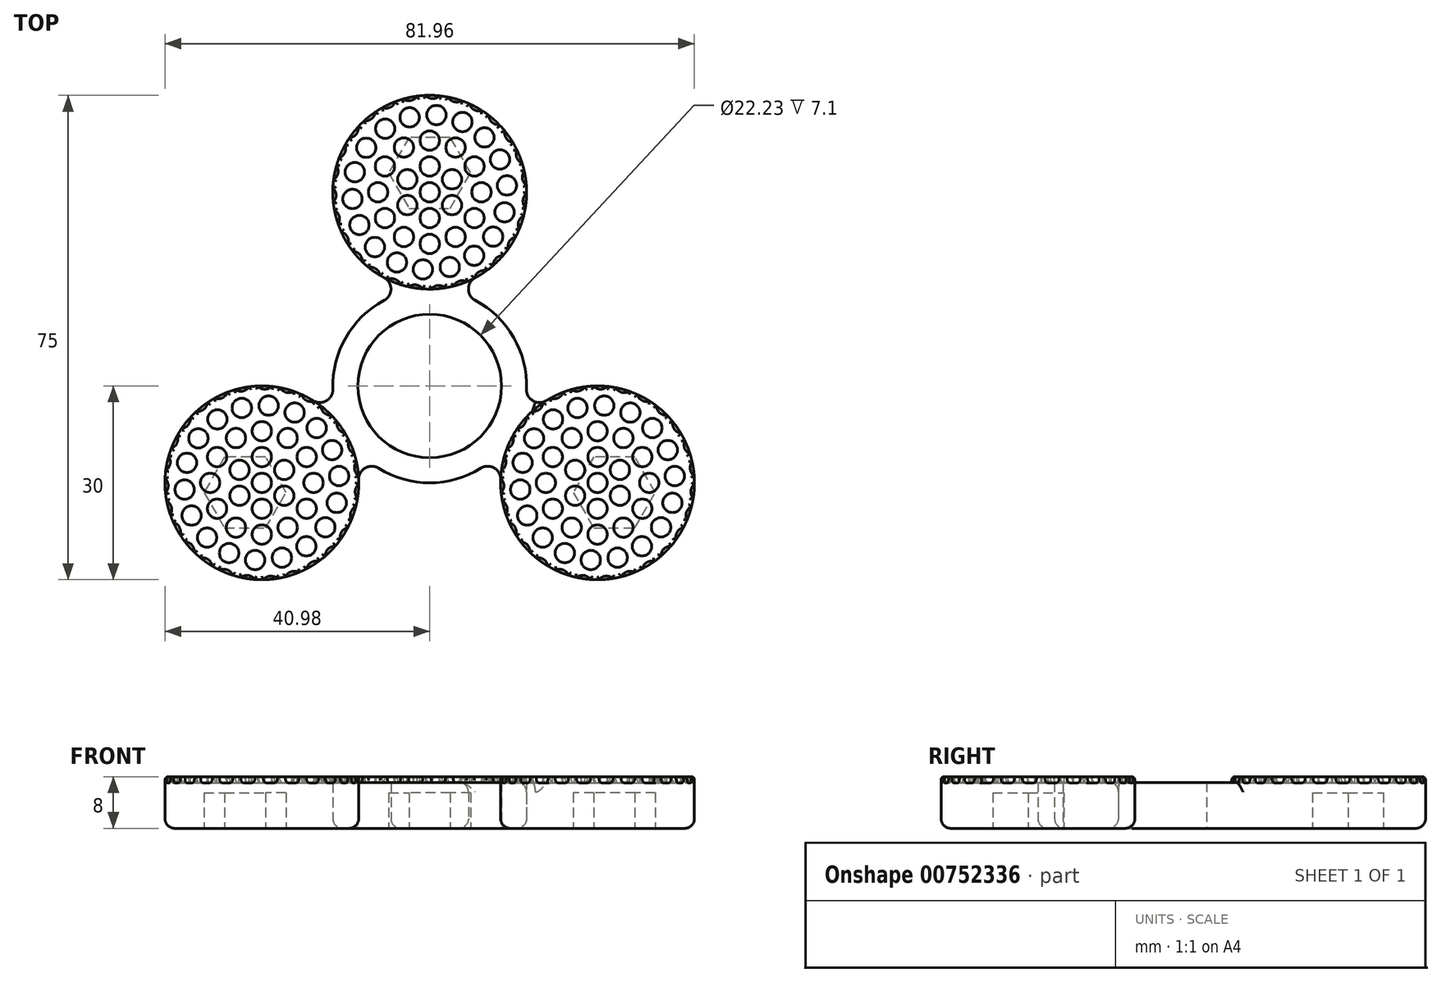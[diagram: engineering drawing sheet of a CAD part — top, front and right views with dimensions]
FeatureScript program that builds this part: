
annotation { "Feature Type Name" : "Feature", "Feature Type Description" : "" }
export const myFeature = defineFeature(function(context is Context, id is Id, definition is map)
    precondition{}
    {
        {
            var Q0;
            Q0=qCreatedBy(makeId("Top.planeOp"),FACE);
            var sketch = newSketch(context, id + "F0", { "sketchPlane" : qUnion([Q0])});
            skCircle(sketch, "E0", {"center": v(0, 0) * mm, "radius": 15 * mm});
            skSolve(sketch);
        }
        {
            var Q0;
            Q0 = qSketchRegion(id + "F0", true);
            extrude(context, id + "F1", {"entities" : qUnion([Q0]), "depth" : 8 * mm, "offsetDistance" : 25 * mm});
        }
        {
            var Q0;
            Q0=makeQuery(id+"F1.opExtrude","CAP_FACE",FACE,{"disambiguationData":[OSD([sQuery(id+"F0.wireOp",EDGE,"E0")])],"isStart":false});
            var sketch = newSketch(context, id + "F2", { "sketchPlane" : qUnion([Q0])});
            skCircle(sketch, "E1", {"center": v(0, 0) * mm, "radius": 1.5 * mm});
            skCircle(sketch, "E2", {"center": v(0, 4) * mm, "radius": 1.5 * mm});
            skCircle(sketch, "E3.1.0", {"center": v(-3.46, 2) * mm, "radius": 1.5 * mm});
            skCircle(sketch, "E3.2.0", {"center": v(-3.46, -2) * mm, "radius": 1.5 * mm});
            skCircle(sketch, "E3.3.0", {"center": v(0, -4) * mm, "radius": 1.5 * mm});
            skCircle(sketch, "E3.4.0", {"center": v(3.46, -2) * mm, "radius": 1.5 * mm});
            skCircle(sketch, "E3.5.0", {"center": v(3.46, 2) * mm, "radius": 1.5 * mm});
            skCircle(sketch, "E4", {"center": v(4, 6.93) * mm, "radius": 1.5 * mm});
            skCircle(sketch, "E5.1.0", {"center": v(0, 8) * mm, "radius": 1.5 * mm});
            skCircle(sketch, "E5.2.0", {"center": v(-4, 6.93) * mm, "radius": 1.5 * mm});
            skCircle(sketch, "E5.3.0", {"center": v(-6.93, 4) * mm, "radius": 1.5 * mm});
            skCircle(sketch, "E5.4.0", {"center": v(-8, 0) * mm, "radius": 1.5 * mm});
            skCircle(sketch, "E5.5.0", {"center": v(-6.93, -4) * mm, "radius": 1.5 * mm});
            skCircle(sketch, "E5.6.0", {"center": v(-4, -6.93) * mm, "radius": 1.5 * mm});
            skCircle(sketch, "E5.7.0", {"center": v(0, -8) * mm, "radius": 1.5 * mm});
            skCircle(sketch, "E5.8.0", {"center": v(4, -6.93) * mm, "radius": 1.5 * mm});
            skCircle(sketch, "E5.9.0", {"center": v(6.93, -4) * mm, "radius": 1.5 * mm});
            skCircle(sketch, "E5.10.0", {"center": v(8, 0) * mm, "radius": 1.5 * mm});
            skCircle(sketch, "E5.11.0", {"center": v(6.93, 4) * mm, "radius": 1.5 * mm});
            skCircle(sketch, "E6", {"center": v(8.49, 8.49) * mm, "radius": 1.5 * mm});
            skCircle(sketch, "E7.1.0", {"center": v(5.07, 10.88) * mm, "radius": 1.5 * mm});
            skCircle(sketch, "E7.2.0", {"center": v(1.05, 11.95) * mm, "radius": 1.5 * mm});
            skCircle(sketch, "E7.3.0", {"center": v(-3.1, 11.6) * mm, "radius": 1.5 * mm});
            skCircle(sketch, "E7.4.0", {"center": v(-6.88, 9.83) * mm, "radius": 1.5 * mm});
            skCircle(sketch, "E7.5.0", {"center": v(-9.83, 6.88) * mm, "radius": 1.5 * mm});
            skCircle(sketch, "E7.6.0", {"center": v(-11.6, 3.1) * mm, "radius": 1.5 * mm});
            skCircle(sketch, "E7.7.0", {"center": v(-11.95, -1.05) * mm, "radius": 1.5 * mm});
            skCircle(sketch, "E7.8.0", {"center": v(-10.88, -5.07) * mm, "radius": 1.5 * mm});
            skCircle(sketch, "E7.9.0", {"center": v(-8.49, -8.49) * mm, "radius": 1.5 * mm});
            skCircle(sketch, "E7.10.0", {"center": v(-5.07, -10.88) * mm, "radius": 1.5 * mm});
            skCircle(sketch, "E7.11.0", {"center": v(-1.05, -11.95) * mm, "radius": 1.5 * mm});
            skCircle(sketch, "E7.12.0", {"center": v(3.1, -11.6) * mm, "radius": 1.5 * mm});
            skCircle(sketch, "E7.13.0", {"center": v(6.88, -9.83) * mm, "radius": 1.5 * mm});
            skCircle(sketch, "E7.14.0", {"center": v(9.83, -6.88) * mm, "radius": 1.5 * mm});
            skCircle(sketch, "E7.15.0", {"center": v(11.6, -3.1) * mm, "radius": 1.5 * mm});
            skCircle(sketch, "E7.16.0", {"center": v(11.95, 1.05) * mm, "radius": 1.5 * mm});
            skCircle(sketch, "E7.17.0", {"center": v(10.88, 5.07) * mm, "radius": 1.5 * mm});
            skArc(sketch, "E8", {"start": v(12.88, 7.7) * mm, "mid": v(12.29, 8.6) * mm, "end": v(11.63, 9.47) * mm});
            skArc(sketch, "E9", {"start": v(11.63, 9.47) * mm, "mid": v(11.88, 8.32) * mm, "end": v(12.88, 7.7) * mm});
            skArc(sketch, "E10.1.0", {"start": v(9.14, 11.9) * mm, "mid": v(9.64, 10.83) * mm, "end": v(10.75, 10.46) * mm});
            skArc(sketch, "E10.1.1", {"start": v(10.75, 10.46) * mm, "mid": v(9.97, 11.2) * mm, "end": v(9.14, 11.9) * mm});
            skArc(sketch, "E10.2.0", {"start": v(6.15, 13.68) * mm, "mid": v(6.88, 12.76) * mm, "end": v(8.05, 12.66) * mm});
            skArc(sketch, "E10.2.1", {"start": v(8.05, 12.66) * mm, "mid": v(7.12, 13.2) * mm, "end": v(6.15, 13.68) * mm});
            skArc(sketch, "E10.3.0", {"start": v(2.83, 14.73) * mm, "mid": v(3.75, 14) * mm, "end": v(4.92, 14.17) * mm});
            skArc(sketch, "E10.3.1", {"start": v(4.92, 14.17) * mm, "mid": v(3.88, 14.49) * mm, "end": v(2.83, 14.73) * mm});
            skArc(sketch, "E10.4.0", {"start": v(-0.65, 14.99) * mm, "mid": v(0.42, 14.5) * mm, "end": v(1.52, 14.92) * mm});
            skArc(sketch, "E10.4.1", {"start": v(1.52, 14.92) * mm, "mid": v(0.44, 15) * mm, "end": v(-0.65, 14.99) * mm});
            skArc(sketch, "E10.5.0", {"start": v(-4.08, 14.43) * mm, "mid": v(-2.93, 14.2) * mm, "end": v(-1.97, 14.87) * mm});
            skArc(sketch, "E10.5.1", {"start": v(-1.97, 14.87) * mm, "mid": v(-3.03, 14.7) * mm, "end": v(-4.08, 14.43) * mm});
            skArc(sketch, "E10.6.0", {"start": v(-7.3, 13.1) * mm, "mid": v(-6.13, 13.14) * mm, "end": v(-5.34, 14.02) * mm});
            skArc(sketch, "E10.6.1", {"start": v(-5.34, 14.02) * mm, "mid": v(-6.34, 13.6) * mm, "end": v(-7.3, 13.1) * mm});
            skArc(sketch, "E10.7.0", {"start": v(-10.13, 11.06) * mm, "mid": v(-9, 11.37) * mm, "end": v(-8.43, 12.4) * mm});
            skArc(sketch, "E10.7.1", {"start": v(-8.43, 12.4) * mm, "mid": v(-9.3, 11.77) * mm, "end": v(-10.13, 11.06) * mm});
            skArc(sketch, "E10.8.0", {"start": v(-12.4, 8.43) * mm, "mid": v(-11.37, 9) * mm, "end": v(-11.06, 10.13) * mm});
            skArc(sketch, "E10.8.1", {"start": v(-11.06, 10.13) * mm, "mid": v(-11.77, 9.3) * mm, "end": v(-12.4, 8.43) * mm});
            skArc(sketch, "E10.9.0", {"start": v(-14.02, 5.34) * mm, "mid": v(-13.14, 6.13) * mm, "end": v(-13.1, 7.3) * mm});
            skArc(sketch, "E10.9.1", {"start": v(-13.1, 7.3) * mm, "mid": v(-13.6, 6.34) * mm, "end": v(-14.02, 5.34) * mm});
            skArc(sketch, "E10.10.0", {"start": v(-14.87, 1.97) * mm, "mid": v(-14.2, 2.93) * mm, "end": v(-14.43, 4.08) * mm});
            skArc(sketch, "E10.10.1", {"start": v(-14.43, 4.08) * mm, "mid": v(-14.7, 3.03) * mm, "end": v(-14.87, 1.97) * mm});
            skArc(sketch, "E10.11.0", {"start": v(-14.92, -1.52) * mm, "mid": v(-14.5, -0.42) * mm, "end": v(-14.99, 0.65) * mm});
            skArc(sketch, "E10.11.1", {"start": v(-14.99, 0.65) * mm, "mid": v(-15, -0.44) * mm, "end": v(-14.92, -1.52) * mm});
            skArc(sketch, "E10.12.0", {"start": v(-14.17, -4.92) * mm, "mid": v(-14, -3.75) * mm, "end": v(-14.73, -2.83) * mm});
            skArc(sketch, "E10.12.1", {"start": v(-14.73, -2.83) * mm, "mid": v(-14.49, -3.88) * mm, "end": v(-14.17, -4.92) * mm});
            skArc(sketch, "E10.13.0", {"start": v(-12.66, -8.05) * mm, "mid": v(-12.76, -6.88) * mm, "end": v(-13.68, -6.15) * mm});
            skArc(sketch, "E10.13.1", {"start": v(-13.68, -6.15) * mm, "mid": v(-13.2, -7.12) * mm, "end": v(-12.66, -8.05) * mm});
            skArc(sketch, "E10.14.0", {"start": v(-10.46, -10.75) * mm, "mid": v(-10.83, -9.64) * mm, "end": v(-11.9, -9.14) * mm});
            skArc(sketch, "E10.14.1", {"start": v(-11.9, -9.14) * mm, "mid": v(-11.2, -9.97) * mm, "end": v(-10.46, -10.75) * mm});
            skArc(sketch, "E10.15.0", {"start": v(-7.7, -12.88) * mm, "mid": v(-8.32, -11.88) * mm, "end": v(-9.47, -11.63) * mm});
            skArc(sketch, "E10.15.1", {"start": v(-9.47, -11.63) * mm, "mid": v(-8.6, -12.29) * mm, "end": v(-7.7, -12.88) * mm});
            skArc(sketch, "E10.16.0", {"start": v(-4.52, -14.3) * mm, "mid": v(-5.35, -13.48) * mm, "end": v(-6.53, -13.5) * mm});
            skArc(sketch, "E10.16.1", {"start": v(-6.53, -13.5) * mm, "mid": v(-5.54, -13.94) * mm, "end": v(-4.52, -14.3) * mm});
            skArc(sketch, "E10.17.0", {"start": v(-1.1, -14.96) * mm, "mid": v(-2.1, -14.35) * mm, "end": v(-3.24, -14.65) * mm});
            skArc(sketch, "E10.17.1", {"start": v(-3.24, -14.65) * mm, "mid": v(-2.17, -14.84) * mm, "end": v(-1.1, -14.96) * mm});
            skArc(sketch, "E10.18.0", {"start": v(2.38, -14.8) * mm, "mid": v(1.26, -14.44) * mm, "end": v(0.23, -15) * mm});
            skArc(sketch, "E10.18.1", {"start": v(0.23, -15) * mm, "mid": v(1.3, -14.94) * mm, "end": v(2.38, -14.8) * mm});
            skArc(sketch, "E10.19.0", {"start": v(5.73, -13.86) * mm, "mid": v(4.56, -13.76) * mm, "end": v(3.68, -14.54) * mm});
            skArc(sketch, "E10.19.1", {"start": v(3.68, -14.54) * mm, "mid": v(4.72, -14.24) * mm, "end": v(5.73, -13.86) * mm});
            skArc(sketch, "E10.20.0", {"start": v(8.77, -12.17) * mm, "mid": v(7.61, -12.34) * mm, "end": v(6.93, -13.3) * mm});
            skArc(sketch, "E10.20.1", {"start": v(6.93, -13.3) * mm, "mid": v(7.87, -12.77) * mm, "end": v(8.77, -12.17) * mm});
            skArc(sketch, "E10.21.0", {"start": v(11.34, -9.81) * mm, "mid": v(10.25, -10.25) * mm, "end": v(9.81, -11.34) * mm});
            skArc(sketch, "E10.21.1", {"start": v(9.81, -11.34) * mm, "mid": v(10.6, -10.6) * mm, "end": v(11.34, -9.81) * mm});
            skArc(sketch, "E10.22.0", {"start": v(13.3, -6.93) * mm, "mid": v(12.34, -7.61) * mm, "end": v(12.17, -8.77) * mm});
            skArc(sketch, "E10.22.1", {"start": v(12.17, -8.77) * mm, "mid": v(12.77, -7.87) * mm, "end": v(13.3, -6.93) * mm});
            skArc(sketch, "E10.23.0", {"start": v(14.54, -3.68) * mm, "mid": v(13.76, -4.56) * mm, "end": v(13.86, -5.73) * mm});
            skArc(sketch, "E10.23.1", {"start": v(13.86, -5.73) * mm, "mid": v(14.24, -4.72) * mm, "end": v(14.54, -3.68) * mm});
            skArc(sketch, "E10.24.0", {"start": v(15, -0.23) * mm, "mid": v(14.44, -1.26) * mm, "end": v(14.8, -2.38) * mm});
            skArc(sketch, "E10.24.1", {"start": v(14.8, -2.38) * mm, "mid": v(14.94, -1.3) * mm, "end": v(15, -0.23) * mm});
            skArc(sketch, "E10.25.0", {"start": v(14.65, 3.24) * mm, "mid": v(14.35, 2.1) * mm, "end": v(14.96, 1.1) * mm});
            skArc(sketch, "E10.25.1", {"start": v(14.96, 1.1) * mm, "mid": v(14.84, 2.17) * mm, "end": v(14.65, 3.24) * mm});
            skArc(sketch, "E10.26.0", {"start": v(13.5, 6.53) * mm, "mid": v(13.48, 5.35) * mm, "end": v(14.3, 4.52) * mm});
            skArc(sketch, "E10.26.1", {"start": v(14.3, 4.52) * mm, "mid": v(13.94, 5.54) * mm, "end": v(13.5, 6.53) * mm});
            skSolve(sketch);
        }
        {
            var Q0;
            Q0 = qSketchRegion(id + "F2", true);
            extrude(context, id + "F3", {"entities" : qUnion([Q0]), "operationType" : NewBodyOperationType.REMOVE, "oppositeDirection" : true, "depth" : 1 * mm, "offsetDistance" : 25 * mm});
        }
        {
            var Q0;
            Q0=makeQuery(id+"F3.boolean.opBoolean","COPY",FACE,{"derivedFrom":makeQuery(id+"F3.opExtrude","CAP_FACE",FACE,{"disambiguationData":[OSD([sQuery(id+"F2.wireOp",EDGE,"E7.5.0")])],"isStart":false})});
            var Q1;
            Q1=makeQuery(id+"F3.boolean.opBoolean","COPY",FACE,{"derivedFrom":makeQuery(id+"F3.opExtrude","CAP_FACE",FACE,{"disambiguationData":[OSD([sQuery(id+"F2.wireOp",EDGE,"E7.4.0")])],"isStart":false})});
            var Q2;
            Q2=makeQuery(id+"F3.boolean.opBoolean","COPY",FACE,{"derivedFrom":makeQuery(id+"F3.opExtrude","CAP_FACE",FACE,{"disambiguationData":[OSD([sQuery(id+"F2.wireOp",EDGE,"E7.3.0")])],"isStart":false})});
            var Q3;
            Q3=makeQuery(id+"F3.boolean.opBoolean","COPY",FACE,{"derivedFrom":makeQuery(id+"F3.opExtrude","CAP_FACE",FACE,{"disambiguationData":[OSD([sQuery(id+"F2.wireOp",EDGE,"E7.2.0")])],"isStart":false})});
            var Q4;
            Q4=makeQuery(id+"F3.boolean.opBoolean","COPY",FACE,{"derivedFrom":makeQuery(id+"F3.opExtrude","CAP_FACE",FACE,{"disambiguationData":[OSD([sQuery(id+"F2.wireOp",EDGE,"E7.1.0")])],"isStart":false})});
            var Q5;
            Q5=makeQuery(id+"F3.boolean.opBoolean","COPY",FACE,{"derivedFrom":makeQuery(id+"F3.opExtrude","CAP_FACE",FACE,{"disambiguationData":[OSD([sQuery(id+"F2.wireOp",EDGE,"E6")])],"isStart":false})});
            var Q6;
            Q6=makeQuery(id+"F3.boolean.opBoolean","COPY",FACE,{"derivedFrom":makeQuery(id+"F3.opExtrude","CAP_FACE",FACE,{"disambiguationData":[OSD([sQuery(id+"F2.wireOp",EDGE,"E7.17.0")])],"isStart":false})});
            var Q7;
            Q7=makeQuery(id+"F3.boolean.opBoolean","COPY",FACE,{"derivedFrom":makeQuery(id+"F3.opExtrude","CAP_FACE",FACE,{"disambiguationData":[OSD([sQuery(id+"F2.wireOp",EDGE,"E7.16.0")])],"isStart":false})});
            var Q8;
            Q8=makeQuery(id+"F3.boolean.opBoolean","COPY",FACE,{"derivedFrom":makeQuery(id+"F3.opExtrude","CAP_FACE",FACE,{"disambiguationData":[OSD([sQuery(id+"F2.wireOp",EDGE,"E7.15.0")])],"isStart":false})});
            var Q9;
            Q9=makeQuery(id+"F3.boolean.opBoolean","COPY",FACE,{"derivedFrom":makeQuery(id+"F3.opExtrude","CAP_FACE",FACE,{"disambiguationData":[OSD([sQuery(id+"F2.wireOp",EDGE,"E7.14.0")])],"isStart":false})});
            var Q10;
            Q10=makeQuery(id+"F3.boolean.opBoolean","COPY",FACE,{"derivedFrom":makeQuery(id+"F3.opExtrude","CAP_FACE",FACE,{"disambiguationData":[OSD([sQuery(id+"F2.wireOp",EDGE,"E7.13.0")])],"isStart":false})});
            var Q11;
            Q11=makeQuery(id+"F3.boolean.opBoolean","COPY",FACE,{"derivedFrom":makeQuery(id+"F3.opExtrude","CAP_FACE",FACE,{"disambiguationData":[OSD([sQuery(id+"F2.wireOp",EDGE,"E7.12.0")])],"isStart":false})});
            var Q12;
            Q12=makeQuery(id+"F3.boolean.opBoolean","COPY",FACE,{"derivedFrom":makeQuery(id+"F3.opExtrude","CAP_FACE",FACE,{"disambiguationData":[OSD([sQuery(id+"F2.wireOp",EDGE,"E7.11.0")])],"isStart":false})});
            var Q13;
            Q13=makeQuery(id+"F3.boolean.opBoolean","COPY",FACE,{"derivedFrom":makeQuery(id+"F3.opExtrude","CAP_FACE",FACE,{"disambiguationData":[OSD([sQuery(id+"F2.wireOp",EDGE,"E7.10.0")])],"isStart":false})});
            var Q14;
            Q14=makeQuery(id+"F3.boolean.opBoolean","COPY",FACE,{"derivedFrom":makeQuery(id+"F3.opExtrude","CAP_FACE",FACE,{"disambiguationData":[OSD([sQuery(id+"F2.wireOp",EDGE,"E7.9.0")])],"isStart":false})});
            var Q15;
            Q15=makeQuery(id+"F3.boolean.opBoolean","COPY",FACE,{"derivedFrom":makeQuery(id+"F3.opExtrude","CAP_FACE",FACE,{"disambiguationData":[OSD([sQuery(id+"F2.wireOp",EDGE,"E7.8.0")])],"isStart":false})});
            var Q16;
            Q16=makeQuery(id+"F3.boolean.opBoolean","COPY",FACE,{"derivedFrom":makeQuery(id+"F3.opExtrude","CAP_FACE",FACE,{"disambiguationData":[OSD([sQuery(id+"F2.wireOp",EDGE,"E7.7.0")])],"isStart":false})});
            var Q17;
            Q17=makeQuery(id+"F3.boolean.opBoolean","COPY",FACE,{"derivedFrom":makeQuery(id+"F3.opExtrude","CAP_FACE",FACE,{"disambiguationData":[OSD([sQuery(id+"F2.wireOp",EDGE,"E7.6.0")])],"isStart":false})});
            var Q18;
            Q18=makeQuery(id+"F3.boolean.opBoolean","COPY",FACE,{"derivedFrom":makeQuery(id+"F3.opExtrude","CAP_FACE",FACE,{"disambiguationData":[OSD([sQuery(id+"F2.wireOp",EDGE,"E5.3.0")])],"isStart":false})});
            var Q19;
            Q19=makeQuery(id+"F3.boolean.opBoolean","COPY",FACE,{"derivedFrom":makeQuery(id+"F3.opExtrude","CAP_FACE",FACE,{"disambiguationData":[OSD([sQuery(id+"F2.wireOp",EDGE,"E5.2.0")])],"isStart":false})});
            var Q20;
            Q20=makeQuery(id+"F3.boolean.opBoolean","COPY",FACE,{"derivedFrom":makeQuery(id+"F3.opExtrude","CAP_FACE",FACE,{"disambiguationData":[OSD([sQuery(id+"F2.wireOp",EDGE,"E5.1.0")])],"isStart":false})});
            var Q21;
            Q21=makeQuery(id+"F3.boolean.opBoolean","COPY",FACE,{"derivedFrom":makeQuery(id+"F3.opExtrude","CAP_FACE",FACE,{"disambiguationData":[OSD([sQuery(id+"F2.wireOp",EDGE,"E4")])],"isStart":false})});
            var Q22;
            Q22=makeQuery(id+"F3.boolean.opBoolean","COPY",FACE,{"derivedFrom":makeQuery(id+"F3.opExtrude","CAP_FACE",FACE,{"disambiguationData":[OSD([sQuery(id+"F2.wireOp",EDGE,"E5.11.0")])],"isStart":false})});
            var Q23;
            Q23=makeQuery(id+"F3.boolean.opBoolean","COPY",FACE,{"derivedFrom":makeQuery(id+"F3.opExtrude","CAP_FACE",FACE,{"disambiguationData":[OSD([sQuery(id+"F2.wireOp",EDGE,"E5.10.0")])],"isStart":false})});
            var Q24;
            Q24=makeQuery(id+"F3.boolean.opBoolean","COPY",FACE,{"derivedFrom":makeQuery(id+"F3.opExtrude","CAP_FACE",FACE,{"disambiguationData":[OSD([sQuery(id+"F2.wireOp",EDGE,"E5.9.0")])],"isStart":false})});
            var Q25;
            Q25=makeQuery(id+"F3.boolean.opBoolean","COPY",FACE,{"derivedFrom":makeQuery(id+"F3.opExtrude","CAP_FACE",FACE,{"disambiguationData":[OSD([sQuery(id+"F2.wireOp",EDGE,"E5.8.0")])],"isStart":false})});
            var Q26;
            Q26=makeQuery(id+"F3.boolean.opBoolean","COPY",FACE,{"derivedFrom":makeQuery(id+"F3.opExtrude","CAP_FACE",FACE,{"disambiguationData":[OSD([sQuery(id+"F2.wireOp",EDGE,"E5.7.0")])],"isStart":false})});
            var Q27;
            Q27=makeQuery(id+"F3.boolean.opBoolean","COPY",FACE,{"derivedFrom":makeQuery(id+"F3.opExtrude","CAP_FACE",FACE,{"disambiguationData":[OSD([sQuery(id+"F2.wireOp",EDGE,"E5.6.0")])],"isStart":false})});
            var Q28;
            Q28=makeQuery(id+"F3.boolean.opBoolean","COPY",FACE,{"derivedFrom":makeQuery(id+"F3.opExtrude","CAP_FACE",FACE,{"disambiguationData":[OSD([sQuery(id+"F2.wireOp",EDGE,"E5.5.0")])],"isStart":false})});
            var Q29;
            Q29=makeQuery(id+"F3.boolean.opBoolean","COPY",FACE,{"derivedFrom":makeQuery(id+"F3.opExtrude","CAP_FACE",FACE,{"disambiguationData":[OSD([sQuery(id+"F2.wireOp",EDGE,"E5.4.0")])],"isStart":false})});
            var Q30;
            Q30=makeQuery(id+"F3.boolean.opBoolean","COPY",FACE,{"derivedFrom":makeQuery(id+"F3.opExtrude","CAP_FACE",FACE,{"disambiguationData":[OSD([sQuery(id+"F2.wireOp",EDGE,"E3.1.0")])],"isStart":false})});
            var Q31;
            Q31=makeQuery(id+"F3.boolean.opBoolean","COPY",FACE,{"derivedFrom":makeQuery(id+"F3.opExtrude","CAP_FACE",FACE,{"disambiguationData":[OSD([sQuery(id+"F2.wireOp",EDGE,"E2")])],"isStart":false})});
            var Q32;
            Q32=makeQuery(id+"F3.boolean.opBoolean","COPY",FACE,{"derivedFrom":makeQuery(id+"F3.opExtrude","CAP_FACE",FACE,{"disambiguationData":[OSD([sQuery(id+"F2.wireOp",EDGE,"E3.5.0")])],"isStart":false})});
            var Q33;
            Q33=makeQuery(id+"F3.boolean.opBoolean","COPY",FACE,{"derivedFrom":makeQuery(id+"F3.opExtrude","CAP_FACE",FACE,{"disambiguationData":[OSD([sQuery(id+"F2.wireOp",EDGE,"E3.4.0")])],"isStart":false})});
            var Q34;
            Q34=makeQuery(id+"F3.boolean.opBoolean","COPY",FACE,{"derivedFrom":makeQuery(id+"F3.opExtrude","CAP_FACE",FACE,{"disambiguationData":[OSD([sQuery(id+"F2.wireOp",EDGE,"E3.3.0")])],"isStart":false})});
            var Q35;
            Q35=makeQuery(id+"F3.boolean.opBoolean","COPY",FACE,{"derivedFrom":makeQuery(id+"F3.opExtrude","CAP_FACE",FACE,{"disambiguationData":[OSD([sQuery(id+"F2.wireOp",EDGE,"E3.2.0")])],"isStart":false})});
            var Q36;
            Q36=makeQuery(id+"F3.boolean.opBoolean","COPY",FACE,{"derivedFrom":makeQuery(id+"F3.opExtrude","CAP_FACE",FACE,{"disambiguationData":[OSD([sQuery(id+"F2.wireOp",EDGE,"E1")])],"isStart":false})});
            var Q37;
            Q37=makeQuery(id+"F3.boolean.opBoolean","COPY",EDGE,{"derivedFrom":makeQuery(id+"F3.opExtrude","CAP_EDGE",EDGE,{"disambiguationData":[OSD([sQuery(id+"F2.wireOp",EDGE,"E10.20.0")])],"isStart":false})});
            var Q38;
            Q38=makeQuery(id+"F3.boolean.opBoolean","COPY",EDGE,{"derivedFrom":makeQuery(id+"F3.opExtrude","CAP_EDGE",EDGE,{"disambiguationData":[OSD([sQuery(id+"F2.wireOp",EDGE,"E10.19.0")])],"isStart":false})});
            var Q39;
            Q39=makeQuery(id+"F3.boolean.opBoolean","COPY",EDGE,{"derivedFrom":makeQuery(id+"F3.opExtrude","CAP_EDGE",EDGE,{"disambiguationData":[OSD([sQuery(id+"F2.wireOp",EDGE,"E10.21.0")])],"isStart":false})});
            var Q40;
            Q40=makeQuery(id+"F3.boolean.opBoolean","COPY",EDGE,{"derivedFrom":makeQuery(id+"F3.opExtrude","CAP_EDGE",EDGE,{"disambiguationData":[OSD([sQuery(id+"F2.wireOp",EDGE,"E10.22.0")])],"isStart":false})});
            var Q41;
            Q41=makeQuery(id+"F3.boolean.opBoolean","COPY",EDGE,{"derivedFrom":makeQuery(id+"F3.opExtrude","CAP_EDGE",EDGE,{"disambiguationData":[OSD([sQuery(id+"F2.wireOp",EDGE,"E10.23.0")])],"isStart":false})});
            var Q42;
            Q42=makeQuery(id+"F3.boolean.opBoolean","COPY",EDGE,{"derivedFrom":makeQuery(id+"F3.opExtrude","CAP_EDGE",EDGE,{"disambiguationData":[OSD([sQuery(id+"F2.wireOp",EDGE,"E10.24.0")])],"isStart":false})});
            var Q43;
            Q43=makeQuery(id+"F3.boolean.opBoolean","COPY",EDGE,{"derivedFrom":makeQuery(id+"F3.opExtrude","CAP_EDGE",EDGE,{"disambiguationData":[OSD([sQuery(id+"F2.wireOp",EDGE,"E10.25.0")])],"isStart":false})});
            var Q44;
            Q44=makeQuery(id+"F3.boolean.opBoolean","COPY",EDGE,{"derivedFrom":makeQuery(id+"F3.opExtrude","CAP_EDGE",EDGE,{"disambiguationData":[OSD([sQuery(id+"F2.wireOp",EDGE,"E10.26.0")])],"isStart":false})});
            var Q45;
            Q45=makeQuery(id+"F3.boolean.opBoolean","COPY",EDGE,{"derivedFrom":makeQuery(id+"F3.opExtrude","CAP_EDGE",EDGE,{"disambiguationData":[OSD([sQuery(id+"F2.wireOp",EDGE,"E9")])],"isStart":false})});
            var Q46;
            Q46=makeQuery(id+"F3.boolean.opBoolean","COPY",EDGE,{"derivedFrom":makeQuery(id+"F3.opExtrude","CAP_EDGE",EDGE,{"disambiguationData":[OSD([sQuery(id+"F2.wireOp",EDGE,"E10.1.0")])],"isStart":false})});
            var Q47;
            Q47=makeQuery(id+"F3.boolean.opBoolean","COPY",EDGE,{"derivedFrom":makeQuery(id+"F3.opExtrude","CAP_EDGE",EDGE,{"disambiguationData":[OSD([sQuery(id+"F2.wireOp",EDGE,"E10.2.0")])],"isStart":false})});
            var Q48;
            Q48=makeQuery(id+"F3.boolean.opBoolean","COPY",EDGE,{"derivedFrom":makeQuery(id+"F3.opExtrude","CAP_EDGE",EDGE,{"disambiguationData":[OSD([sQuery(id+"F2.wireOp",EDGE,"E10.3.0")])],"isStart":false})});
            var Q49;
            Q49=makeQuery(id+"F3.boolean.opBoolean","COPY",EDGE,{"derivedFrom":makeQuery(id+"F3.opExtrude","CAP_EDGE",EDGE,{"disambiguationData":[OSD([sQuery(id+"F2.wireOp",EDGE,"E10.4.0")])],"isStart":false})});
            var Q50;
            Q50=makeQuery(id+"F3.boolean.opBoolean","COPY",EDGE,{"derivedFrom":makeQuery(id+"F3.opExtrude","CAP_EDGE",EDGE,{"disambiguationData":[OSD([sQuery(id+"F2.wireOp",EDGE,"E10.5.0")])],"isStart":false})});
            var Q51;
            Q51=makeQuery(id+"F3.boolean.opBoolean","COPY",EDGE,{"derivedFrom":makeQuery(id+"F3.opExtrude","CAP_EDGE",EDGE,{"disambiguationData":[OSD([sQuery(id+"F2.wireOp",EDGE,"E10.6.0")])],"isStart":false})});
            var Q52;
            Q52=makeQuery(id+"F3.boolean.opBoolean","COPY",EDGE,{"derivedFrom":makeQuery(id+"F3.opExtrude","CAP_EDGE",EDGE,{"disambiguationData":[OSD([sQuery(id+"F2.wireOp",EDGE,"E10.7.0")])],"isStart":false})});
            var Q53;
            Q53=makeQuery(id+"F3.boolean.opBoolean","COPY",EDGE,{"derivedFrom":makeQuery(id+"F3.opExtrude","CAP_EDGE",EDGE,{"disambiguationData":[OSD([sQuery(id+"F2.wireOp",EDGE,"E10.8.0")])],"isStart":false})});
            var Q54;
            Q54=makeQuery(id+"F3.boolean.opBoolean","COPY",EDGE,{"derivedFrom":makeQuery(id+"F3.opExtrude","CAP_EDGE",EDGE,{"disambiguationData":[OSD([sQuery(id+"F2.wireOp",EDGE,"E10.9.0")])],"isStart":false})});
            var Q55;
            Q55=makeQuery(id+"F3.boolean.opBoolean","COPY",EDGE,{"derivedFrom":makeQuery(id+"F3.opExtrude","CAP_EDGE",EDGE,{"disambiguationData":[OSD([sQuery(id+"F2.wireOp",EDGE,"E10.10.0")])],"isStart":false})});
            var Q56;
            Q56=makeQuery(id+"F3.boolean.opBoolean","COPY",EDGE,{"derivedFrom":makeQuery(id+"F3.opExtrude","CAP_EDGE",EDGE,{"disambiguationData":[OSD([sQuery(id+"F2.wireOp",EDGE,"E10.11.0")])],"isStart":false})});
            var Q57;
            Q57=makeQuery(id+"F3.boolean.opBoolean","COPY",EDGE,{"derivedFrom":makeQuery(id+"F3.opExtrude","CAP_EDGE",EDGE,{"disambiguationData":[OSD([sQuery(id+"F2.wireOp",EDGE,"E10.12.0")])],"isStart":false})});
            var Q58;
            Q58=makeQuery(id+"F3.boolean.opBoolean","COPY",EDGE,{"derivedFrom":makeQuery(id+"F3.opExtrude","CAP_EDGE",EDGE,{"disambiguationData":[OSD([sQuery(id+"F2.wireOp",EDGE,"E10.13.0")])],"isStart":false})});
            var Q59;
            Q59=makeQuery(id+"F3.boolean.opBoolean","COPY",EDGE,{"derivedFrom":makeQuery(id+"F3.opExtrude","CAP_EDGE",EDGE,{"disambiguationData":[OSD([sQuery(id+"F2.wireOp",EDGE,"E10.14.0")])],"isStart":false})});
            var Q60;
            Q60=makeQuery(id+"F3.boolean.opBoolean","COPY",EDGE,{"derivedFrom":makeQuery(id+"F3.opExtrude","CAP_EDGE",EDGE,{"disambiguationData":[OSD([sQuery(id+"F2.wireOp",EDGE,"E10.15.0")])],"isStart":false})});
            var Q61;
            Q61=makeQuery(id+"F3.boolean.opBoolean","COPY",EDGE,{"derivedFrom":makeQuery(id+"F3.opExtrude","CAP_EDGE",EDGE,{"disambiguationData":[OSD([sQuery(id+"F2.wireOp",EDGE,"E10.16.0")])],"isStart":false})});
            var Q62;
            Q62=makeQuery(id+"F3.boolean.opBoolean","COPY",EDGE,{"derivedFrom":makeQuery(id+"F3.opExtrude","CAP_EDGE",EDGE,{"disambiguationData":[OSD([sQuery(id+"F2.wireOp",EDGE,"E10.17.0")])],"isStart":false})});
            var Q63;
            Q63=makeQuery(id+"F3.boolean.opBoolean","COPY",EDGE,{"derivedFrom":makeQuery(id+"F3.opExtrude","CAP_EDGE",EDGE,{"disambiguationData":[OSD([sQuery(id+"F2.wireOp",EDGE,"E10.18.0")])],"isStart":false})});
            fillet(context, id + "F4", {"entities" : qUnion([Q0, Q1, Q2, Q3, Q4, Q5, Q6, Q7, Q8, Q9, Q10, Q11, Q12, Q13, Q14, Q15, Q16, Q17, Q18, Q19, Q20, Q21, Q22, Q23, Q24, Q25, Q26, Q27, Q28, Q29, Q30, Q31, Q32, Q33, Q34, Q35, Q36, Q37, Q38, Q39, Q40, Q41, Q42, Q43, Q44, Q45, Q46, Q47, Q48, Q49, Q50, Q51, Q52, Q53, Q54, Q55, Q56, Q57, Q58, Q59, Q60, Q61, Q62, Q63]), "radius" : .5 * mm, "tangentPropagation" : true, "allowEdgeOverflow" : false});
        }
        {
            var Q0;
            Q0=makeQuery(id+"F1.opExtrude","CAP_FACE",FACE,{"disambiguationData":[OSD([sQuery(id+"F0.wireOp",EDGE,"E0")])],"isStart":false});
            fillet(context, id + "F5", {"entities" : qUnion([Q0]), "radius" : .5 * mm, "tangentPropagation" : true, "allowEdgeOverflow" : false});
        }
        {
            var Q0;
            Q0=qCreatedBy(makeId("Top.planeOp"),FACE);
            var sketch = newSketch(context, id + "F6", { "sketchPlane" : qUnion([Q0])});
            skLineSegment(sketch, "E11", {"start": v(0, -30) * mm, "end": v(0, 15) * mm});
            skSolve(sketch);
        }
        {
            var Q0;
            Q0=qCreatedBy(makeId("Front.planeOp"),FACE);
            cPlane(context, id + "F7", {"entities" : qUnion([Q0]), "cplaneType" : CPlaneType.OFFSET, "offset" : 30 * mm, "width" : 150 * mm, "height" : 150 * mm});
        }
        {
            var Q0;
            Q0=qCreatedBy(id+"F7.planeOp",FACE);
            var sketch = newSketch(context, id + "F8", { "sketchPlane" : qUnion([Q0])});
            skLineSegment(sketch, "E12", {"start": v(0, 0) * mm, "end": v(0, 41.09) * mm});
            skSolve(sketch);
        }
        {
            var Q0;
            Q0=makeQuery(id+"F1.opExtrude","SWEPT_BODY",BODY,{"disambiguationData":[OSD([sQuery(id+"F0.wireOp",EDGE,"E0")])]});
            var Q1;
            Q1=sQuery(id+"F8.wireOp",EDGE,"E12");
            circularPattern(context, id + "F9", {"entities" : qUnion([Q0]), "axis" : qUnion([Q1]), "angle" : 360 * degree, "instanceCount" : 3, "equalSpace" : true, "computeTransformsWithoutBuiltin" : true});
        }
        {
            var Q0;
            Q0=qCreatedBy(makeId("Top.planeOp"),FACE);
            var sketch = newSketch(context, id + "F10", { "sketchPlane" : qUnion([Q0])});
            skCircle(sketch, "E13", {"center": v(0, -30) * mm, "radius": 15 * mm});
            skCircle(sketch, "E14", {"center": v(0, -30) * mm, "radius": 11.11 * mm});
            skSolve(sketch);
        }
        {
            var Q0;
            Q0 = qSketchRegion(id + "F10", true);
            extrude(context, id + "F11", {"entities" : qUnion([Q0]), "operationType" : NewBodyOperationType.ADD, "depth" : 7.1 * mm, "offsetDistance" : 25 * mm});
        }
        {
            var Q0;
            Q0=makeQuery(id+"F11.opExtrude","CAP_FACE",FACE,{"disambiguationData":[OSD([sQuery(id+"F10.wireOp",EDGE,"E13"),sQuery(id+"F10.wireOp",EDGE,"E14")])],"isStart":true});
            var sketch = newSketch(context, id + "F12", { "sketchPlane" : qUnion([Q0])});
            skArc(sketch, "E15", {"start": v(7.06, 16.76) * mm, "mid": v(6, 15) * mm, "end": v(7.06, 13.24) * mm});
            skArc(sketch, "E16.MirrorCS", {"start": v(-7.06, 16.76) * mm, "mid": v(-6, 15) * mm, "end": v(-7.06, 13.24) * mm});
            skArc(sketch, "E17.1.0", {"start": v(15, 30.5) * mm, "mid": v(16, 32.3) * mm, "end": v(18.05, 32.27) * mm});
            skArc(sketch, "E17.1.1", {"start": v(7.93, 42.73) * mm, "mid": v(10, 42.7) * mm, "end": v(10.99, 44.5) * mm});
            skArc(sketch, "E17.2.0", {"start": v(-7.93, 42.73) * mm, "mid": v(-10, 42.7) * mm, "end": v(-10.99, 44.5) * mm});
            skArc(sketch, "E17.2.1", {"start": v(-15, 30.5) * mm, "mid": v(-16, 32.3) * mm, "end": v(-18.05, 32.27) * mm});
            skPoint(sketch, "E17.center", {"position": v(0, 30) * mm});
            skArc(sketch, "E18", {"start": v(-18.05, 32.27) * mm, "mid": v(-13, 37.5) * mm, "end": v(-10.99, 44.5) * mm});
            skArc(sketch, "E19", {"start": v(-7.93, 42.73) * mm, "mid": v(-13, 37.5) * mm, "end": v(-15, 30.5) * mm});
            skArc(sketch, "E20", {"start": v(15, 30.41) * mm, "mid": v(13.01, 37.46) * mm, "end": v(7.93, 42.73) * mm});
            skArc(sketch, "E21", {"start": v(-7.06, 16.76) * mm, "mid": v(0, 15) * mm, "end": v(7.06, 16.76) * mm});
            skArc(sketch, "E22", {"start": v(7.06, 13.24) * mm, "mid": v(0, 15) * mm, "end": v(-7.06, 13.24) * mm});
            skArc(sketch, "E23", {"start": v(10.99, 44.5) * mm, "mid": v(13, 37.5) * mm, "end": v(18.05, 32.27) * mm});
            skSolve(sketch);
        }
        {
            var Q0;
            Q0 = qSketchRegion(id + "F12", true);
            extrude(context, id + "F13", {"entities" : qUnion([Q0]), "operationType" : NewBodyOperationType.ADD, "oppositeDirection" : true, "depth" : 7.1 * mm, "offsetDistance" : 25 * mm});
        }
        {
            var Q0;
            Q0=makeQuery(id+"F1.opExtrude","CAP_EDGE",EDGE,{"disambiguationData":[OSD([sQuery(id+"F0.wireOp",EDGE,"E0")])],"isStart":true});
            fillet(context, id + "F14", {"entities" : qUnion([Q0]), "radius" : 1.5 * mm, "tangentPropagation" : true, "allowEdgeOverflow" : false});
        }
        {
            var Q0;
            {var subQ2=sQuery(id+"F10.wireOp",EDGE,"E13");var subQ5=sQuery(id+"F12.wireOp",EDGE,"E17.1.1");Q0=makeQuery(id+"F13.boolean.opBoolean","SPLIT",EDGE,{"disambiguationData":[TD([makeQuery(id+"F13.opExtrude","SWEPT_FACE",FACE,{"disambiguationData":[OSD([subQ5])]})])],"derivedFrom":makeQuery(id+"F11.opExtrude","CAP_EDGE",EDGE,{"disambiguationData":[OSD([subQ2])],"isStart":false})});}
            var Q1;
            {var subQ2=sQuery(id+"F12.wireOp",EDGE,"E15");var subQ3=sQuery(id+"F10.wireOp",EDGE,"E13");Q1=makeQuery(id+"F13.boolean.opBoolean","SPLIT",EDGE,{"disambiguationData":[TD([makeQuery(id+"F13.opExtrude","SWEPT_FACE",FACE,{"disambiguationData":[OSD([subQ2])]})])],"derivedFrom":makeQuery(id+"F11.opExtrude","CAP_EDGE",EDGE,{"disambiguationData":[OSD([subQ3])],"isStart":false})});}
            var Q2;
            {var subQ0=sQuery(id+"F12.wireOp",EDGE,"E16.MirrorCS");var subQ5=sQuery(id+"F10.wireOp",EDGE,"E13");Q2=makeQuery(id+"F13.boolean.opBoolean","SPLIT",EDGE,{"disambiguationData":[TD([makeQuery(id+"F13.opExtrude","SWEPT_FACE",FACE,{"disambiguationData":[OSD([subQ0])]})])],"derivedFrom":makeQuery(id+"F11.opExtrude","CAP_EDGE",EDGE,{"disambiguationData":[OSD([subQ5])],"isStart":false})});}
            fillet(context, id + "F15", {"entities" : qUnion([Q0, Q1, Q2]), "radius" : 1.5 * mm, "tangentPropagation" : true, "allowEdgeOverflow" : false});
        }
        {
            var Q0;
            {var subQ0=sQuery(id+"F12.wireOp",EDGE,"E19");var subQ1=sQuery(id+"F12.wireOp",EDGE,"E18");var subQ2=sQuery(id+"F12.wireOp",EDGE,"E23");var subQ3=sQuery(id+"F12.wireOp",EDGE,"E20");var subQ4=sQuery(id+"F12.wireOp",EDGE,"E22");var subQ5=sQuery(id+"F12.wireOp",EDGE,"E21");var subQ6=makeQuery(id+"F1.opExtrude","CAP_FACE",FACE,{"disambiguationData":[OSD([sQuery(id+"F0.wireOp",EDGE,"E0")])],"isStart":true});Q0=makeQuery(id+"F13.boolean.opBoolean","MERGE",FACE,{"derivedFrom":[subQ6,makeQuery(id+"F9.opPattern","COPY",FACE,{"derivedFrom":subQ6,"instanceName":"1"}),makeQuery(id+"F9.opPattern","COPY",FACE,{"derivedFrom":subQ6,"instanceName":"2"}),makeQuery(id+"F11.opExtrude","CAP_FACE",FACE,{"disambiguationData":[OSD([sQuery(id+"F10.wireOp",EDGE,"E13"),sQuery(id+"F10.wireOp",EDGE,"E14")])],"isStart":true}),makeQuery(id+"F13.opExtrude","CAP_FACE",FACE,{"disambiguationData":[OSD([sQuery(id+"F12.wireOp",EDGE,"E15"),subQ5,subQ4])],"isStart":true}),makeQuery(id+"F13.opExtrude","CAP_FACE",FACE,{"disambiguationData":[OSD([sQuery(id+"F12.wireOp",EDGE,"E16.MirrorCS"),subQ5,subQ4])],"isStart":true}),makeQuery(id+"F13.opExtrude","CAP_FACE",FACE,{"disambiguationData":[OSD([sQuery(id+"F12.wireOp",EDGE,"E17.1.0"),subQ3,subQ2])],"isStart":true}),makeQuery(id+"F13.opExtrude","CAP_FACE",FACE,{"disambiguationData":[OSD([sQuery(id+"F12.wireOp",EDGE,"E17.1.1"),subQ3,subQ2])],"isStart":true}),makeQuery(id+"F13.opExtrude","CAP_FACE",FACE,{"disambiguationData":[OSD([sQuery(id+"F12.wireOp",EDGE,"E17.2.0"),subQ1,subQ0])],"isStart":true}),makeQuery(id+"F13.opExtrude","CAP_FACE",FACE,{"disambiguationData":[OSD([sQuery(id+"F12.wireOp",EDGE,"E17.2.1"),subQ1,subQ0])],"isStart":true})]});}
            var sketch = newSketch(context, id + "F16", { "sketchPlane" : qUnion([Q0])});
            skCircle(sketch, "E24.cCircle", {"center": v(0, -3) * mm, "radius": 5.5 * mm, "construction": true});
            skLineSegment(sketch, "E24.0", {"start": v(3.18, -8.5) * mm, "end": v(-3.18, -8.5) * mm});
            skLineSegment(sketch, "E24.1", {"start": v(-3.18, -8.5) * mm, "end": v(-6.35, -3) * mm});
            skLineSegment(sketch, "E24.2", {"start": v(-6.35, -3) * mm, "end": v(-3.18, 2.5) * mm});
            skLineSegment(sketch, "E24.3", {"start": v(-3.18, 2.5) * mm, "end": v(3.18, 2.5) * mm});
            skLineSegment(sketch, "E24.4", {"start": v(3.18, 2.5) * mm, "end": v(6.35, -3) * mm});
            skLineSegment(sketch, "E24.5", {"start": v(6.35, -3) * mm, "end": v(3.18, -8.5) * mm});
            skPoint(sketch, "E24.0.midPoint", {"position": v(0, -8.5) * mm});
            skLineSegment(sketch, "E25.1.0", {"start": v(22.23, 46.5) * mm, "end": v(25.4, 52) * mm});
            skLineSegment(sketch, "E25.1.1", {"start": v(25.4, 52) * mm, "end": v(31.75, 52) * mm});
            skPoint(sketch, "E25.1.2", {"position": v(33.34, 49.25) * mm});
            skCircle(sketch, "E25.1.3", {"center": v(28.58, 46.5) * mm, "radius": 5.5 * mm, "construction": true});
            skLineSegment(sketch, "E25.1.4", {"start": v(31.75, 41) * mm, "end": v(25.4, 41) * mm});
            skLineSegment(sketch, "E25.1.5", {"start": v(25.4, 41) * mm, "end": v(22.23, 46.5) * mm});
            skLineSegment(sketch, "E25.1.6", {"start": v(31.75, 52) * mm, "end": v(34.93, 46.5) * mm});
            skLineSegment(sketch, "E25.1.7", {"start": v(34.93, 46.5) * mm, "end": v(31.75, 41) * mm});
            skLineSegment(sketch, "E25.2.0", {"start": v(-25.4, 41) * mm, "end": v(-31.75, 41) * mm});
            skLineSegment(sketch, "E25.2.1", {"start": v(-31.75, 41) * mm, "end": v(-34.93, 46.5) * mm});
            skPoint(sketch, "E25.2.2", {"position": v(-33.34, 49.25) * mm});
            skCircle(sketch, "E25.2.3", {"center": v(-28.58, 46.5) * mm, "radius": 5.5 * mm, "construction": true});
            skLineSegment(sketch, "E25.2.4", {"start": v(-25.4, 52) * mm, "end": v(-22.23, 46.5) * mm});
            skLineSegment(sketch, "E25.2.5", {"start": v(-22.23, 46.5) * mm, "end": v(-25.4, 41) * mm});
            skLineSegment(sketch, "E25.2.6", {"start": v(-34.93, 46.5) * mm, "end": v(-31.75, 52) * mm});
            skLineSegment(sketch, "E25.2.7", {"start": v(-31.75, 52) * mm, "end": v(-25.4, 52) * mm});
            skPoint(sketch, "E25.center", {"position": v(0, 30) * mm});
            skSolve(sketch);
        }
        {
            var Q0;
            Q0 = qSketchRegion(id + "F16", true);
            extrude(context, id + "F17", {"entities" : qUnion([Q0]), "operationType" : NewBodyOperationType.REMOVE, "oppositeDirection" : true, "depth" : 5.5 * mm, "offsetDistance" : 25 * mm});
        }
    });
